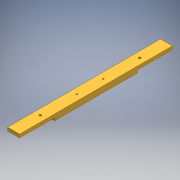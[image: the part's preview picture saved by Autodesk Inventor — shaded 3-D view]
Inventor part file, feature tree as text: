
AUTODESK INVENTOR PART (.ipt)
format: ipt  version: 2016 (Build 200138000, 138)  size: 147,456 bytes
history: native  units: mm
features: sketch x5, extrude x3, hole x2
ambient origin geometry x8: Origin, YZ Plane, XZ Plane, XY Plane, X Axis, Y Axis, Z Axis, Center Point
bodies: Solid1 (feature_tree)
feature tree (10):
  sketch  "Sketch1"  dims[d0=16.0mm d1=111.075mm]
  sketch  "Sketch2"  dims[d2=55.5375mm d3=8.0mm]
  sketch  "Sketch3"  dims[d4=80.0mm d5=40.0mm]
  extrude  "baseExtrusion"  Depth=111.075mm
  hole  "xyStageAttach_m5"  [1 undecoded]
  hole  "pedestalAttach_m6"  [1 undecoded]
  extrude  "Extrusion2"  Depth=10.0mm
  extrude  "Extrusion3"  Depth=8.0mm
  sketch  "Sketch4"  dims[d6=10.0mm d7=175.0mm]
  sketch  "Sketch5"  dims[d8=10.0mm d9=175.0mm d10=300.0mm d11=150.0mm d12=10.0mm d13=0.0mm d14=4.134mm d15=10.0mm d16=4.0mm d17=2.0mm d18=90.0deg d19=14.2mm d20=20.594885mm d21=6.6mm d22=12.0mm d23=18.0mm d24=4.8mm d25=90.0deg d26=17.1mm d27=20.594885mm d28=125.0mm d29=125.0mm d30=8.0mm d31=0.0mm d32=150.0mm d33=75.0mm d34=20.0mm d35=10.0mm d36=8.0mm d37=0.0mm]
note: 2 required parameter values undecoded (feature->parameter linkage not recoverable at this tier; creation-order binding heuristic only, values carry confidence <= 0.55)
